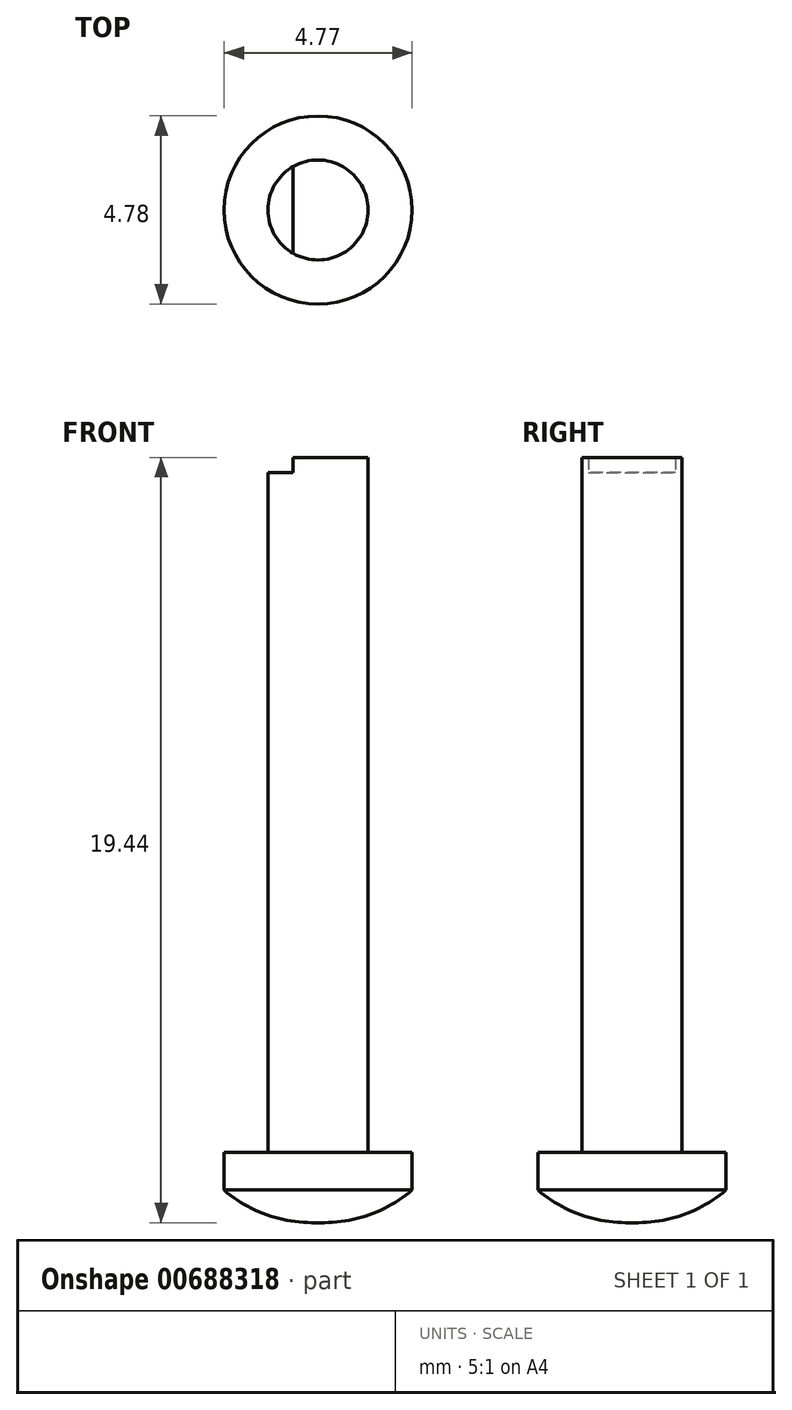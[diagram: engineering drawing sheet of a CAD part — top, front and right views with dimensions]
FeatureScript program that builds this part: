
annotation { "Feature Type Name" : "Feature", "Feature Type Description" : "" }
export const myFeature = defineFeature(function(context is Context, id is Id, definition is map)
    precondition{}
    {
        {
            var Q0;
            Q0=qCreatedBy(makeId("Front.planeOp"),FACE);
            var sketch = newSketch(context, id + "F0", { "sketchPlane" : qUnion([Q0])});
            skLineSegment(sketch, "E0.bottom", {"start": v(-39.45, 53.55) * mm, "end": v(-38.18, 53.55) * mm});
            skLineSegment(sketch, "E0.top", {"start": v(-39.45, 36.28) * mm, "end": v(-38.18, 36.28) * mm});
            skLineSegment(sketch, "E0.left", {"start": v(-39.45, 53.55) * mm, "end": v(-39.45, 36.28) * mm});
            skLineSegment(sketch, "E0.right", {"start": v(-38.18, 53.55) * mm, "end": v(-38.18, 36.28) * mm});
            skLineSegment(sketch, "E1", {"start": v(-38.18, 36.28) * mm, "end": v(-40.56, 36.28) * mm});
            skLineSegment(sketch, "E2", {"start": v(-40.56, 35.97) * mm, "end": v(-40.56, 36.28) * mm});
            skLineSegment(sketch, "E3", {"start": v(-38.18, 35.13) * mm, "end": v(-38.18, 36.28) * mm});
            skLineSegment(sketch, "E4", {"start": v(-40.56, 35.97) * mm, "end": v(-40.56, 35.33) * mm});
            skLineSegment(sketch, "E5", {"start": v(-38.18, 35.13) * mm, "end": v(-38.18, 34.5) * mm});
            skLineSegment(sketch, "E6", {"start": v(-38.18, 34.5) * mm, "end": v(-38.34, 34.5) * mm});
            skArc(sketch, "E7", {"start": v(-40.56, 35.33) * mm, "mid": v(-39.52, 34.72) * mm, "end": v(-38.34, 34.5) * mm});
            skSolve(sketch);
        }
        {
            var Q0;
            {var subQ0=sQuery(id+"F0.wireOp",EDGE,"2s3XmbjV-6D1X-21uM-oQFG-9KiFPrlXN8ep");Q0=makeQuery(id+"F0.imprint","IMPRINT",FACE,{"disambiguationData":[TD([[makeQuery(id+"F0.imprint","IMPRINT",EDGE,{"derivedFrom":subQ0}),1.0]])]});}
            var Q1;
            Q1=makeQuery(id+"F0.imprint","IMPRINT",FACE,{"disambiguationData":[TD([[makeQuery(id+"F0.imprint","IMPRINT",EDGE,{"derivedFrom":sQuery(id+"F0.wireOp",EDGE,"E0.bottom")}),-1.0]])]});
            var Q2;
            {var subQ0=sQuery(id+"F0.wireOp",EDGE,"E2");Q2=makeQuery(id+"F0.imprint","IMPRINT",FACE,{"disambiguationData":[TD([[makeQuery(id+"F0.imprint","IMPRINT",EDGE,{"derivedFrom":subQ0}),-1.0]])]});}
            var Q3;
            Q3=sQuery(id+"F0.wireOp",EDGE,"E0.right");
            revolve(context, id + "F1", {"entities" : qUnion([Q0, Q1, Q2]), "axis" : qUnion([Q3]), "revolveType" : RevolveType.FULL});
        }
        {
            var Q0;
            Q0=makeQuery(id+"F1.opRevolve","SWEPT_FACE",FACE,{"disambiguationData":[OSD([sQuery(id+"F0.wireOp",EDGE,"E0.bottom")])]});
            var sketch = newSketch(context, id + "F2", { "sketchPlane" : qUnion([Q0])});
            skLineSegment(sketch, "E8", {"start": v(-38.18, 0) * mm, "end": v(-38.8, 0) * mm});
            skLineSegment(sketch, "E9", {"start": v(-38.8, 0) * mm, "end": v(-38.8, 1.1) * mm});
            skLineSegment(sketch, "E10", {"start": v(-38.8, 1.1) * mm, "end": v(-38.8, -1.1) * mm});
            skSolve(sketch);
        }
        {
            var Q0;
            {var subQ0=sQuery(id+"F2.wireOp",EDGE,"E10");var subQ1=makeQuery(id+"F2.imprint","IMPRINT",VERTEX,{"derivedFrom":subQ0});Q0=makeQuery(id+"F2.imprint","IMPRINT",FACE,{"disambiguationData":[TD([[makeQuery(id+"F2.imprint","IMPRINT",EDGE,{"disambiguationData":[TD([[subQ1,1.0]])],"derivedFrom":subQ0}),1.0]])]});}
            extrude(context, id + "F3", {"entities" : qUnion([Q0]), "operationType" : NewBodyOperationType.ADD, "depth" : 0.38 * mm, "offsetDistance" : 25.4 * mm});
        }
    });
